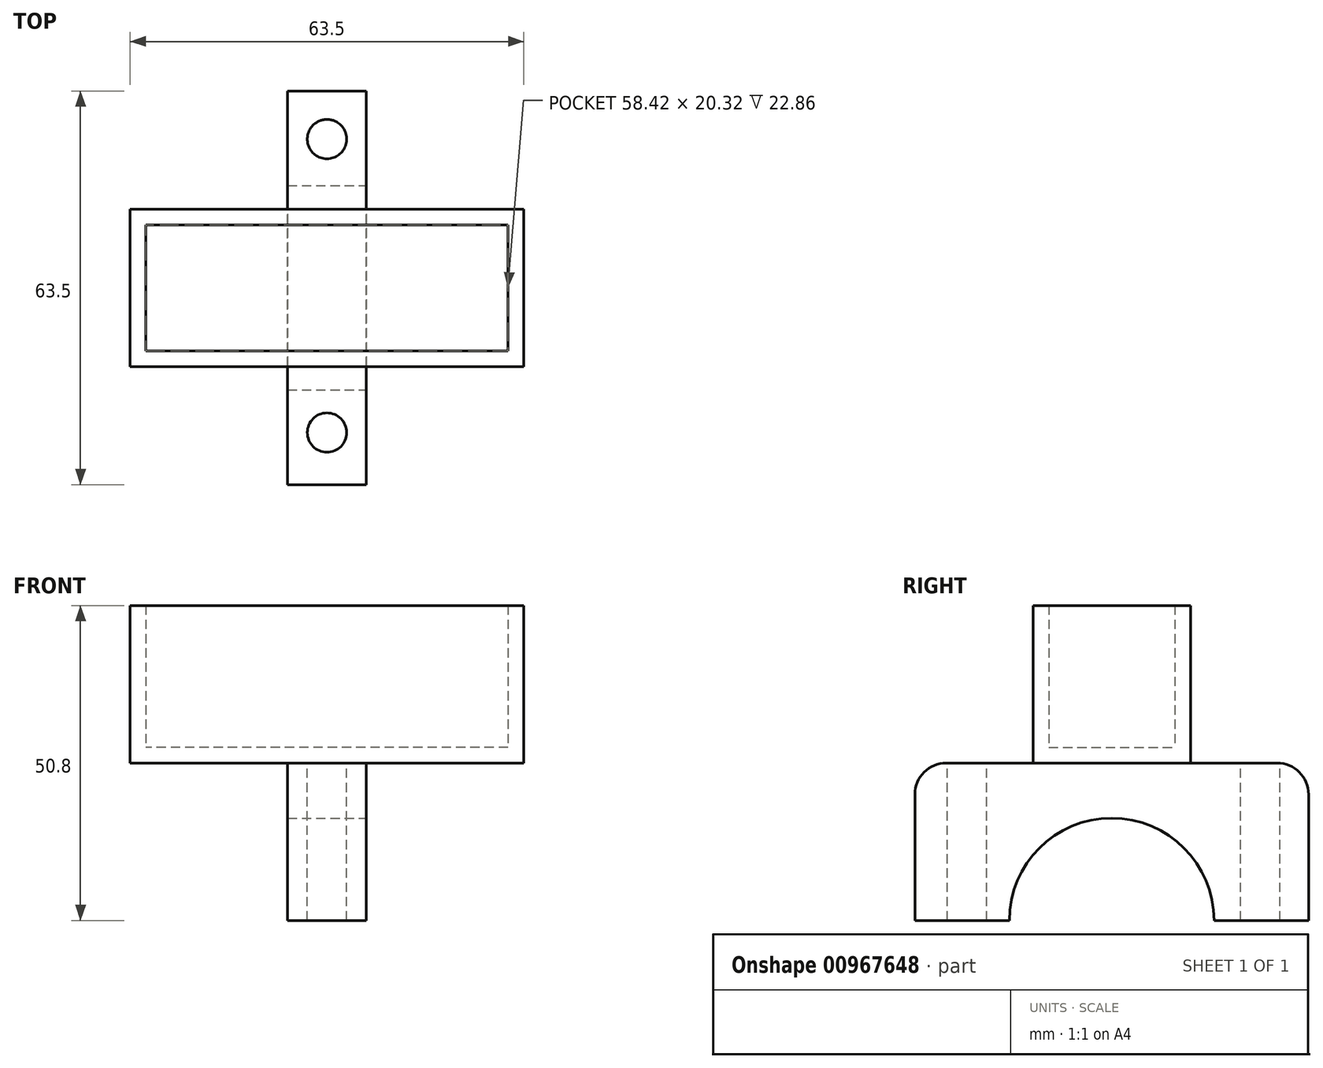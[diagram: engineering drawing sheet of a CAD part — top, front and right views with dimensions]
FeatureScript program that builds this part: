
annotation { "Feature Type Name" : "Feature", "Feature Type Description" : "" }
export const myFeature = defineFeature(function(context is Context, id is Id, definition is map)
    precondition{}
    {
        {
            var Q0;
            Q0=qCreatedBy(makeId("Top.planeOp"),FACE);
            var sketch = newSketch(context, id + "F0", { "sketchPlane" : qUnion([Q0])});
            skLineSegment(sketch, "E0.bottom", {"start": v(31.75, -12.7) * mm, "end": v(-31.75, -12.7) * mm});
            skLineSegment(sketch, "E0.top", {"start": v(31.75, 12.7) * mm, "end": v(-31.75, 12.7) * mm});
            skLineSegment(sketch, "E0.left", {"start": v(31.75, -12.7) * mm, "end": v(31.75, 12.7) * mm});
            skLineSegment(sketch, "E0.right", {"start": v(-31.75, -12.7) * mm, "end": v(-31.75, 12.7) * mm});
            skPoint(sketch, "E0.middle", {"position": v(0, 0) * mm});
            skSolve(sketch);
        }
        {
            var Q0;
            Q0=makeQuery(id+"F0.imprint","IMPRINT",FACE,{"disambiguationData":[TD([[makeQuery(id+"F0.imprint","IMPRINT",EDGE,{"derivedFrom":sQuery(id+"F0.wireOp",EDGE,"E0.bottom")}),-1.0]])]});
            extrude(context, id + "F1", {"entities" : qUnion([Q0]), "depth" : 25.4 * mm, "offsetDistance" : 25.4 * mm});
        }
        {
            var Q0;
            Q0=makeQuery(id+"F1.opExtrude","CAP_FACE",FACE,{"disambiguationData":[OSD([sQuery(id+"F0.wireOp",EDGE,"E0.bottom"),sQuery(id+"F0.wireOp",EDGE,"E0.top"),sQuery(id+"F0.wireOp",EDGE,"E0.left"),sQuery(id+"F0.wireOp",EDGE,"E0.right")])],"isStart":false});
            shell(context, id + "F2", {"entities" : qUnion([Q0]), "thickness" : 2.54 * mm});
        }
        {
            var Q0;
            Q0=makeQuery(id+"F1.opExtrude","CAP_FACE",FACE,{"disambiguationData":[OSD([sQuery(id+"F0.wireOp",EDGE,"E0.bottom"),sQuery(id+"F0.wireOp",EDGE,"E0.top"),sQuery(id+"F0.wireOp",EDGE,"E0.left"),sQuery(id+"F0.wireOp",EDGE,"E0.right")])],"isStart":true});
            var sketch = newSketch(context, id + "F3", { "sketchPlane" : qUnion([Q0])});
            skLineSegment(sketch, "E1.bottom", {"start": v(6.35, 31.75) * mm, "end": v(-6.35, 31.75) * mm});
            skLineSegment(sketch, "E1.top", {"start": v(6.35, -31.75) * mm, "end": v(-6.35, -31.75) * mm});
            skLineSegment(sketch, "E1.left", {"start": v(6.35, 31.75) * mm, "end": v(6.35, -31.75) * mm});
            skLineSegment(sketch, "E1.right", {"start": v(-6.35, 31.75) * mm, "end": v(-6.35, -31.75) * mm});
            skPoint(sketch, "E1.middle", {"position": v(0, 0) * mm});
            skSolve(sketch);
        }
        {
            var Q0;
            {var subQ0=sQuery(id+"F3.wireOp",EDGE,"E1.bottom");Q0=makeQuery(id+"F3.imprint","IMPRINT",FACE,{"disambiguationData":[TD([[makeQuery(id+"F3.imprint","IMPRINT",EDGE,{"derivedFrom":subQ0}),1.0]])]});}
            var Q1;
            {var subQ0=sQuery(id+"F3.wireOp",EDGE,"E1.top");Q1=makeQuery(id+"F3.imprint","IMPRINT",FACE,{"disambiguationData":[TD([[makeQuery(id+"F3.imprint","IMPRINT",EDGE,{"derivedFrom":subQ0}),-1.0]])]});}
            var Q2;
            {var subQ0=sQuery(id+"F3.wireOp",EDGE,"E1.left");var subQ1=makeQuery(id+"F1.opExtrude","CAP_EDGE",EDGE,{"disambiguationData":[OSD([sQuery(id+"F0.wireOp",EDGE,"E0.bottom")])],"isStart":true});var subQ2=makeQuery(id+"F3.imprint","INTERSECT",VERTEX,{"derivedFrom":[subQ1,subQ0]});Q2=makeQuery(id+"F3.imprint","IMPRINT",FACE,{"disambiguationData":[TD([[makeQuery(id+"F3.imprint","IMPRINT",EDGE,{"disambiguationData":[TD([[subQ2,-1.0]])],"derivedFrom":subQ0}),-1.0]])]});}
            extrude(context, id + "F4", {"entities" : qUnion([Q0, Q1, Q2]), "operationType" : NewBodyOperationType.ADD, "depth" : 25.4 * mm, "offsetDistance" : 25.4 * mm});
        }
        {
            var Q0;
            Q0=makeQuery(id+"F4.opExtrude","SWEPT_FACE",FACE,{"disambiguationData":[OSD([sQuery(id+"F3.wireOp",EDGE,"E1.left")])]});
            var sketch = newSketch(context, id + "F5", { "sketchPlane" : qUnion([Q0])});
            skCircle(sketch, "E2", {"center": v(0, -25.4) * mm, "radius": 16.5 * mm});
            skSolve(sketch);
        }
        {
            var Q0;
            {var subQ0=sQuery(id+"F5.wireOp",EDGE,"E2");var subQ1=makeQuery(id+"F4.opExtrude","CAP_EDGE",EDGE,{"disambiguationData":[OSD([sQuery(id+"F3.wireOp",EDGE,"E1.left")])],"isStart":false});var subQ2=makeQuery(id+"F5.imprint","INTERSECT",VERTEX,{"disambiguationData":[OD(0.0)],"derivedFrom":[subQ1,subQ0]});Q0=makeQuery(id+"F5.imprint","IMPRINT",FACE,{"disambiguationData":[TD([[makeQuery(id+"F5.imprint","IMPRINT",EDGE,{"disambiguationData":[TD([[subQ2,1.0]])],"derivedFrom":subQ0}),1.0]])]});}
            extrude(context, id + "F6", {"entities" : qUnion([Q0]), "operationType" : NewBodyOperationType.REMOVE, "endBound" : BoundingType.UP_TO_NEXT, "oppositeDirection" : true, "depth" : 25.4 * mm, "offsetDistance" : 25.4 * mm});
        }
        {
            var Q0;
            Q0=makeQuery(id+"F4.opExtrude","CAP_EDGE",EDGE,{"disambiguationData":[OSD([sQuery(id+"F3.wireOp",EDGE,"E1.top")])],"isStart":true});
            fillet(context, id + "F7", {"entities" : qUnion([Q0]), "radius" : 5.08 * mm, "tangentPropagation" : true, "allowEdgeOverflow" : false});
        }
        {
            var Q0;
            Q0=makeQuery(id+"F4.opExtrude","CAP_EDGE",EDGE,{"disambiguationData":[OSD([sQuery(id+"F3.wireOp",EDGE,"E1.bottom")])],"isStart":true});
            fillet(context, id + "F8", {"entities" : qUnion([Q0]), "radius" : 5.08 * mm, "tangentPropagation" : true, "allowEdgeOverflow" : false});
        }
        {
            var Q0;
            {var subQ0=sQuery(id+"F3.wireOp",EDGE,"E1.top");var subQ1=sQuery(id+"F3.wireOp",EDGE,"E1.left");var subQ2=sQuery(id+"F0.wireOp",EDGE,"E0.top");var subQ3=sQuery(id+"F3.wireOp",EDGE,"E1.right");Q0=makeQuery(id+"F4.boolean.opBoolean","SPLIT",FACE,{"disambiguationData":[TD([makeQuery(id+"F1.opExtrude","SWEPT_FACE",FACE,{"disambiguationData":[OSD([subQ2])]})])],"derivedFrom":makeQuery(id+"F4.opExtrude","CAP_FACE",FACE,{"disambiguationData":[OSD([sQuery(id+"F3.wireOp",EDGE,"E1.bottom"),subQ0,subQ1,subQ3])],"isStart":true})});}
            var sketch = newSketch(context, id + "F9", { "sketchPlane" : qUnion([Q0])});
            skPoint(sketch, "E3", {"position": v(0, 23.97) * mm});
            skPoint(sketch, "E4", {"position": v(0, -23.36) * mm});
            skSolve(sketch);
        }
        {
            var Q0;
            Q0=sQuery(id+"F9.wireOp",VERTEX,"E3");
            var Q1;
            Q1=sQuery(id+"F9.wireOp",VERTEX,"E4");
            var Q2;
            Q2=makeQuery(id+"F1.opExtrude","SWEPT_BODY",BODY,{"disambiguationData":[OSD([sQuery(id+"F0.wireOp",EDGE,"E0.bottom"),sQuery(id+"F0.wireOp",EDGE,"E0.top"),sQuery(id+"F0.wireOp",EDGE,"E0.left"),sQuery(id+"F0.wireOp",EDGE,"E0.right")])]});
            hole(context, id + "F10", {"style" : HoleStyle.C_BORE, "endStyle" : HoleEndStyle.THROUGH, "holeDiameter" : 3.17 * mm, "cBoreDiameter" : 6.35 * mm, "cBoreDepth" : 38.1 * mm, "majorDiameter" : 6.35 * mm, "isTappedThrough" : true, "tappedDepth" : 12.7 * mm, "tapClearance" : 3, "locations" : qUnion([Q0, Q1]), "scope" : qUnion([Q2])});
        }
    });
